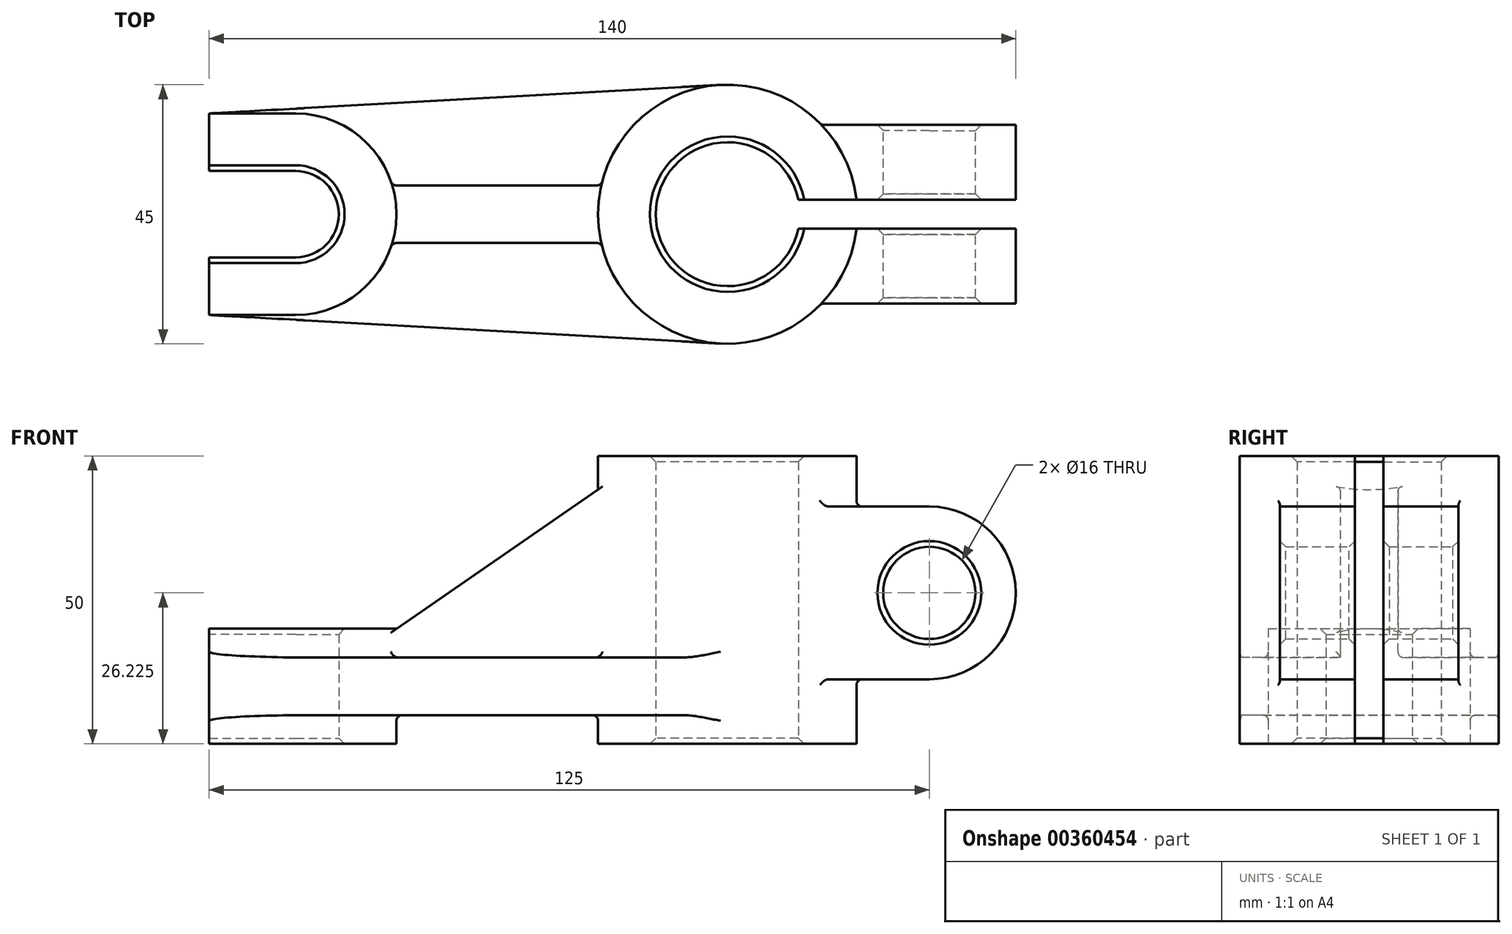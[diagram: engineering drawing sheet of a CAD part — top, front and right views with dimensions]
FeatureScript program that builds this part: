
annotation { "Feature Type Name" : "Feature", "Feature Type Description" : "" }
export const myFeature = defineFeature(function(context is Context, id is Id, definition is map)
    precondition{}
    {
        {
            var Q0;
            Q0=qCreatedBy(makeId("Top.planeOp"),FACE);
            var sketch = newSketch(context, id + "F0", { "sketchPlane" : qUnion([Q0])});
            skCircle(sketch, "E0", {"center": v(0, 0) * mm, "radius": 22.5 * mm});
            skCircle(sketch, "E1", {"center": v(0, 0) * mm, "radius": 12.5 * mm});
            skLineSegment(sketch, "E2", {"start": v(0, 0) * mm, "end": v(-75, 0) * mm, "construction": true});
            skArc(sketch, "E3", {"start": v(-75, -17.5) * mm, "mid": v(-57.5, 0) * mm, "end": v(-75, 17.5) * mm});
            skArc(sketch, "E4", {"start": v(-75, -7.5) * mm, "mid": v(-67.5, 0) * mm, "end": v(-75, 7.5) * mm});
            skLineSegment(sketch, "E5", {"start": v(-75, 17.5) * mm, "end": v(-90, 17.5) * mm});
            skLineSegment(sketch, "E6", {"start": v(-75, 7.5) * mm, "end": v(-90, 7.5) * mm});
            skLineSegment(sketch, "E7", {"start": v(-90, 17.5) * mm, "end": v(-90, 7.5) * mm});
            skLineSegment(sketch, "E8.MirrorCS", {"start": v(-75, -17.5) * mm, "end": v(-90, -17.5) * mm});
            skLineSegment(sketch, "E9.MirrorCS", {"start": v(-90, -17.5) * mm, "end": v(-90, -7.5) * mm});
            skLineSegment(sketch, "E10.MirrorCS", {"start": v(-75, -7.5) * mm, "end": v(-90, -7.5) * mm});
            skLineSegment(sketch, "E11", {"start": v(-90, 17.5) * mm, "end": v(-1.26, 22.46) * mm});
            skLineSegment(sketch, "E12.MirrorCS", {"start": v(-90, -17.5) * mm, "end": v(-1.26, -22.46) * mm});
            skSolve(sketch);
        }
        {
            var Q0;
            Q0 = qSketchRegion(id + "F0", true);
            extrude(context, id + "F1", {"entities" : qUnion([Q0]), "depth" : 10 * mm});
        }
        {
            var Q0;
            Q0=makeQuery(id+"F1.opExtrude","CAP_FACE",FACE,{"disambiguationData":[OSD([sQuery(id+"F0.wireOp",EDGE,"E0"),sQuery(id+"F0.wireOp",EDGE,"E1"),sQuery(id+"F0.wireOp",EDGE,"E4"),sQuery(id+"F0.wireOp",EDGE,"E6"),sQuery(id+"F0.wireOp",EDGE,"E7"),sQuery(id+"F0.wireOp",EDGE,"E9.MirrorCS"),sQuery(id+"F0.wireOp",EDGE,"E10.MirrorCS"),sQuery(id+"F0.wireOp",EDGE,"E11"),sQuery(id+"F0.wireOp",EDGE,"E12.MirrorCS")])],"isStart":false});
            var sketch = newSketch(context, id + "F2", { "sketchPlane" : qUnion([Q0])});
            skArc(sketch, "E13", {"start": v(-75, -17.5) * mm, "mid": v(-57.5, 0) * mm, "end": v(-75, 17.5) * mm});
            skArc(sketch, "E14.0", {"start": v(-75, -7.5) * mm, "mid": v(-67.5, 0) * mm, "end": v(-75, 7.5) * mm});
            skLineSegment(sketch, "E15", {"start": v(-75, 7.5) * mm, "end": v(-90, 7.5) * mm});
            skLineSegment(sketch, "E16", {"start": v(-90, 7.5) * mm, "end": v(-90, 17.5) * mm});
            skLineSegment(sketch, "E17", {"start": v(-90, 17.5) * mm, "end": v(-75, 17.5) * mm});
            skLineSegment(sketch, "E18", {"start": v(-75, 0) * mm, "end": v(0, 0) * mm, "construction": true});
            skLineSegment(sketch, "E19.MirrorCS", {"start": v(-90, -17.5) * mm, "end": v(-75, -17.5) * mm});
            skLineSegment(sketch, "E20.MirrorCS", {"start": v(-90, -7.5) * mm, "end": v(-90, -17.5) * mm});
            skLineSegment(sketch, "E21.MirrorCS", {"start": v(-75, -7.5) * mm, "end": v(-90, -7.5) * mm});
            skSolve(sketch);
        }
        {
            var Q0;
            Q0 = qSketchRegion(id + "F2", true);
            extrude(context, id + "F3", {"entities" : qUnion([Q0]), "operationType" : NewBodyOperationType.ADD, "depth" : 5 * mm, "hasSecondDirection" : true, "secondDirectionOppositeDirection" : true, "secondDirectionDepth" : 15 * mm});
        }
        {
            var Q0;
            Q0=makeQuery(id+"F1.opExtrude","CAP_FACE",FACE,{"disambiguationData":[OSD([sQuery(id+"F0.wireOp",EDGE,"E0"),sQuery(id+"F0.wireOp",EDGE,"E1"),sQuery(id+"F0.wireOp",EDGE,"E4"),sQuery(id+"F0.wireOp",EDGE,"E6"),sQuery(id+"F0.wireOp",EDGE,"E7"),sQuery(id+"F0.wireOp",EDGE,"E9.MirrorCS"),sQuery(id+"F0.wireOp",EDGE,"E10.MirrorCS"),sQuery(id+"F0.wireOp",EDGE,"E11"),sQuery(id+"F0.wireOp",EDGE,"E12.MirrorCS")])],"isStart":false});
            var sketch = newSketch(context, id + "F4", { "sketchPlane" : qUnion([Q0])});
            skCircle(sketch, "E22", {"center": v(0, 0) * mm, "radius": 22.5 * mm});
            skCircle(sketch, "E23", {"center": v(0, 0) * mm, "radius": 12.5 * mm});
            skSolve(sketch);
        }
        {
            var Q0;
            Q0 = qSketchRegion(id + "F4", true);
            extrude(context, id + "F5", {"entities" : qUnion([Q0]), "operationType" : NewBodyOperationType.ADD, "depth" : 35 * mm, "hasSecondDirection" : true, "secondDirectionOppositeDirection" : true, "secondDirectionDepth" : 15 * mm});
        }
        {
            var Q0;
            Q0=qCreatedBy(makeId("Front.planeOp"),FACE);
            var sketch = newSketch(context, id + "F6", { "sketchPlane" : qUnion([Q0])});
            skLineSegment(sketch, "E24", {"start": v(12.5, 36.22) * mm, "end": v(12.5, 6.22) * mm});
            skLineSegment(sketch, "E25", {"start": v(12.5, 36.22) * mm, "end": v(35, 36.22) * mm});
            skLineSegment(sketch, "E26", {"start": v(35, 36.22) * mm, "end": v(35, 21.22) * mm, "construction": true});
            skArc(sketch, "E27", {"start": v(35, 6.22) * mm, "mid": v(50, 21.22) * mm, "end": v(35, 36.22) * mm});
            skCircle(sketch, "E28", {"center": v(35, 21.22) * mm, "radius": 8 * mm});
            skLineSegment(sketch, "E29", {"start": v(35, 6.22) * mm, "end": v(12.5, 6.22) * mm});
            skSolve(sketch);
        }
        {
            var Q0;
            Q0 = qSketchRegion(id + "F6", true);
            extrude(context, id + "F7", {"entities" : qUnion([Q0]), "operationType" : NewBodyOperationType.ADD, "endBound" : BoundingType.SYMMETRIC, "depth" : 31 * mm});
        }
        {
            var Q0;
            Q0=qCreatedBy(makeId("Right.planeOp"),FACE);
            var sketch = newSketch(context, id + "F8", { "sketchPlane" : qUnion([Q0])});
            skPoint(sketch, "E30.0", {"position": v(0, 0) * mm});
            skLineSegment(sketch, "E31", {"start": v(0, 0) * mm, "end": v(0, 60.52) * mm, "construction": true});
            skLineSegment(sketch, "E32", {"start": v(0, 0) * mm, "end": v(0, -26.54) * mm, "construction": true});
            skLineSegment(sketch, "E33.0", {"start": v(-2.5, 45) * mm, "end": v(2.5, 45) * mm});
            skLineSegment(sketch, "E34", {"start": v(0, 45) * mm, "end": v(2.5, 45) * mm});
            skLineSegment(sketch, "E35", {"start": v(2.5, 45) * mm, "end": v(2.5, -5) * mm});
            skLineSegment(sketch, "E36", {"start": v(2.5, -5) * mm, "end": v(-2.5, -5) * mm});
            skLineSegment(sketch, "E37", {"start": v(-2.5, -5) * mm, "end": v(-2.5, 45) * mm});
            skLineSegment(sketch, "E38", {"start": v(-2.5, 45) * mm, "end": v(0, 45) * mm});
            skPoint(sketch, "E39.orphan", {"position": v(-22.5, 45) * mm});
            skPoint(sketch, "E40.orphan", {"position": v(22.5, 45) * mm});
            skSolve(sketch);
        }
        {
            var Q0;
            Q0 = qSketchRegion(id + "F8", true);
            extrude(context, id + "F9", {"entities" : qUnion([Q0]), "operationType" : NewBodyOperationType.REMOVE, "endBound" : BoundingType.THROUGH_ALL, "depth" : 25 * mm});
        }
        {
            var Q0;
            Q0=qCreatedBy(makeId("Front.planeOp"),FACE);
            var sketch = newSketch(context, id + "F10", { "sketchPlane" : qUnion([Q0])});
            skLineSegment(sketch, "E41", {"start": v(-22.5, 39.17) * mm, "end": v(-22.5, 39.22) * mm});
            skLineSegment(sketch, "E42", {"start": v(-57.5, 15) * mm, "end": v(-57.5, 15) * mm});
            skLineSegment(sketch, "E43", {"start": v(-64.73, 10) * mm, "end": v(-22.5, 10) * mm});
            skLineSegment(sketch, "E44", {"start": v(-22.5, 10) * mm, "end": v(-19.86, 10) * mm});
            skLineSegment(sketch, "E45", {"start": v(-19.86, 10) * mm, "end": v(-19.86, 41) * mm});
            skPoint(sketch, "E46.end.orphan", {"position": v(-22.5, 39.22) * mm});
            skLineSegment(sketch, "E47", {"start": v(-19.86, 41) * mm, "end": v(-64.73, 10) * mm});
            skPoint(sketch, "E48.orphan", {"position": v(-57.5, 10) * mm});
            skSolve(sketch);
        }
        {
            var Q0;
            Q0 = qSketchRegion(id + "F10", true);
            extrude(context, id + "F11", {"entities" : qUnion([Q0]), "operationType" : NewBodyOperationType.ADD, "endBound" : BoundingType.SYMMETRIC, "depth" : 10 * mm});
        }
        {
            var Q0;
            Q0=makeQuery(id+"F11.opExtrude","CAP_EDGE",EDGE,{"disambiguationData":[OSD([sQuery(id+"F10.wireOp",EDGE,"E43"),sQuery(id+"F10.wireOp",EDGE,"E44")])],"isStart":false});
            var Q1;
            {var subQ0=makeQuery(id+"F1.opExtrude","CAP_FACE",FACE,{"disambiguationData":[OSD([sQuery(id+"F0.wireOp",EDGE,"E0"),sQuery(id+"F0.wireOp",EDGE,"E1"),sQuery(id+"F0.wireOp",EDGE,"E4"),sQuery(id+"F0.wireOp",EDGE,"E6"),sQuery(id+"F0.wireOp",EDGE,"E7"),sQuery(id+"F0.wireOp",EDGE,"E9.MirrorCS"),sQuery(id+"F0.wireOp",EDGE,"E10.MirrorCS"),sQuery(id+"F0.wireOp",EDGE,"E11"),sQuery(id+"F0.wireOp",EDGE,"E12.MirrorCS")])],"isStart":false});var subQ1=makeQuery(id+"F3.opExtrude","SWEPT_FACE",FACE,{"disambiguationData":[OSD([sQuery(id+"F2.wireOp",EDGE,"E13")])]});Q1=makeQuery(id+"F11.boolean.opBoolean","SPLIT",EDGE,{"disambiguationData":[TD([makeQuery(id+"F3.opExtrude","SWEPT_FACE",FACE,{"disambiguationData":[OSD([sQuery(id+"F2.wireOp",EDGE,"E19.MirrorCS")])]})])],"derivedFrom":makeQuery(id+"F3.boolean.opBoolean","INTERSECT",EDGE,{"derivedFrom":[subQ0,subQ1]})});}
            var Q2;
            {var subQ0=sQuery(id+"F2.wireOp",EDGE,"E19.MirrorCS");var subQ1=sQuery(id+"F2.wireOp",EDGE,"E17");var subQ2=sQuery(id+"F2.wireOp",EDGE,"E13");Q2=makeQuery(id+"F11.boolean.opBoolean","INTERSECT",EDGE,{"derivedFrom":[makeQuery(id+"F3.boolean.opBoolean","SPLIT",FACE,{"disambiguationData":[TD([makeQuery(id+"F3.opExtrude","CAP_FACE",FACE,{"disambiguationData":[OSD([subQ2,sQuery(id+"F2.wireOp",EDGE,"E14.0"),sQuery(id+"F2.wireOp",EDGE,"E15"),sQuery(id+"F2.wireOp",EDGE,"E16"),subQ1,subQ0,sQuery(id+"F2.wireOp",EDGE,"E20.MirrorCS"),sQuery(id+"F2.wireOp",EDGE,"E21.MirrorCS")])],"isStart":false})])],"derivedFrom":makeQuery(id+"F3.opExtrude","SWEPT_FACE",FACE,{"disambiguationData":[OSD([subQ2])]})}),makeQuery(id+"F11.opExtrude","CAP_FACE",FACE,{"disambiguationData":[OSD([sQuery(id+"F10.wireOp",EDGE,"E43"),sQuery(id+"F10.wireOp",EDGE,"E44"),sQuery(id+"F10.wireOp",EDGE,"E45"),sQuery(id+"F10.wireOp",EDGE,"E47")])],"isStart":false})]});}
            var Q3;
            Q3=makeQuery(id+"F11.boolean.opBoolean","INTERSECT",EDGE,{"derivedFrom":[makeQuery(id+"F5.boolean.opBoolean","MERGE",FACE,{"derivedFrom":[makeQuery(id+"F1.opExtrude","SWEPT_FACE",FACE,{"disambiguationData":[OSD([sQuery(id+"F0.wireOp",EDGE,"E0")])]}),makeQuery(id+"F5.opExtrude","SWEPT_FACE",FACE,{"disambiguationData":[OSD([sQuery(id+"F4.wireOp",EDGE,"E22")])]})]}),makeQuery(id+"F11.opExtrude","CAP_FACE",FACE,{"disambiguationData":[OSD([sQuery(id+"F10.wireOp",EDGE,"E43"),sQuery(id+"F10.wireOp",EDGE,"E44"),sQuery(id+"F10.wireOp",EDGE,"E45"),sQuery(id+"F10.wireOp",EDGE,"E47")])],"isStart":false})]});
            var Q4;
            {var subQ0=makeQuery(id+"F5.opExtrude","SWEPT_FACE",FACE,{"disambiguationData":[OSD([sQuery(id+"F4.wireOp",EDGE,"E22")])]});var subQ1=sQuery(id+"F0.wireOp",EDGE,"E12.MirrorCS");var subQ2=sQuery(id+"F0.wireOp",EDGE,"E0");var subQ3=makeQuery(id+"F1.opExtrude","CAP_FACE",FACE,{"disambiguationData":[OSD([subQ2,sQuery(id+"F0.wireOp",EDGE,"E1"),sQuery(id+"F0.wireOp",EDGE,"E4"),sQuery(id+"F0.wireOp",EDGE,"E6"),sQuery(id+"F0.wireOp",EDGE,"E7"),sQuery(id+"F0.wireOp",EDGE,"E9.MirrorCS"),sQuery(id+"F0.wireOp",EDGE,"E10.MirrorCS"),sQuery(id+"F0.wireOp",EDGE,"E11"),subQ1])],"isStart":false});Q4=makeQuery(id+"F11.boolean.opBoolean","SPLIT",EDGE,{"disambiguationData":[TD([makeQuery(id+"F1.opExtrude","SWEPT_FACE",FACE,{"disambiguationData":[OSD([subQ1])]})])],"derivedFrom":makeQuery(id+"F5.boolean.opBoolean","INTERSECT",EDGE,{"derivedFrom":[subQ3,subQ0]})});}
            var Q5;
            {var subQ0=sQuery(id+"F0.wireOp",EDGE,"E11");var subQ1=makeQuery(id+"F5.opExtrude","SWEPT_FACE",FACE,{"disambiguationData":[OSD([sQuery(id+"F4.wireOp",EDGE,"E22")])]});var subQ2=sQuery(id+"F0.wireOp",EDGE,"E0");var subQ3=makeQuery(id+"F1.opExtrude","CAP_FACE",FACE,{"disambiguationData":[OSD([subQ2,sQuery(id+"F0.wireOp",EDGE,"E1"),sQuery(id+"F0.wireOp",EDGE,"E4"),sQuery(id+"F0.wireOp",EDGE,"E6"),sQuery(id+"F0.wireOp",EDGE,"E7"),sQuery(id+"F0.wireOp",EDGE,"E9.MirrorCS"),sQuery(id+"F0.wireOp",EDGE,"E10.MirrorCS"),subQ0,sQuery(id+"F0.wireOp",EDGE,"E12.MirrorCS")])],"isStart":false});Q5=makeQuery(id+"F11.boolean.opBoolean","SPLIT",EDGE,{"disambiguationData":[TD([makeQuery(id+"F1.opExtrude","SWEPT_FACE",FACE,{"disambiguationData":[OSD([subQ0])]})])],"derivedFrom":makeQuery(id+"F5.boolean.opBoolean","INTERSECT",EDGE,{"derivedFrom":[subQ3,subQ1]})});}
            var Q6;
            Q6=makeQuery(id+"F11.boolean.opBoolean","INTERSECT",EDGE,{"derivedFrom":[makeQuery(id+"F5.boolean.opBoolean","MERGE",FACE,{"derivedFrom":[makeQuery(id+"F1.opExtrude","SWEPT_FACE",FACE,{"disambiguationData":[OSD([sQuery(id+"F0.wireOp",EDGE,"E0")])]}),makeQuery(id+"F5.opExtrude","SWEPT_FACE",FACE,{"disambiguationData":[OSD([sQuery(id+"F4.wireOp",EDGE,"E22")])]})]}),makeQuery(id+"F11.opExtrude","CAP_FACE",FACE,{"disambiguationData":[OSD([sQuery(id+"F10.wireOp",EDGE,"E43"),sQuery(id+"F10.wireOp",EDGE,"E44"),sQuery(id+"F10.wireOp",EDGE,"E45"),sQuery(id+"F10.wireOp",EDGE,"E47")])],"isStart":true})]});
            var Q7;
            Q7=makeQuery(id+"F11.opExtrude","CAP_EDGE",EDGE,{"disambiguationData":[OSD([sQuery(id+"F10.wireOp",EDGE,"E43"),sQuery(id+"F10.wireOp",EDGE,"E44")])],"isStart":true});
            var Q8;
            {var subQ0=makeQuery(id+"F1.opExtrude","CAP_FACE",FACE,{"disambiguationData":[OSD([sQuery(id+"F0.wireOp",EDGE,"E0"),sQuery(id+"F0.wireOp",EDGE,"E1"),sQuery(id+"F0.wireOp",EDGE,"E4"),sQuery(id+"F0.wireOp",EDGE,"E6"),sQuery(id+"F0.wireOp",EDGE,"E7"),sQuery(id+"F0.wireOp",EDGE,"E9.MirrorCS"),sQuery(id+"F0.wireOp",EDGE,"E10.MirrorCS"),sQuery(id+"F0.wireOp",EDGE,"E11"),sQuery(id+"F0.wireOp",EDGE,"E12.MirrorCS")])],"isStart":false});var subQ1=makeQuery(id+"F3.opExtrude","SWEPT_FACE",FACE,{"disambiguationData":[OSD([sQuery(id+"F2.wireOp",EDGE,"E13")])]});Q8=makeQuery(id+"F11.boolean.opBoolean","SPLIT",EDGE,{"disambiguationData":[TD([makeQuery(id+"F3.opExtrude","SWEPT_FACE",FACE,{"disambiguationData":[OSD([sQuery(id+"F2.wireOp",EDGE,"E17")])]})])],"derivedFrom":makeQuery(id+"F3.boolean.opBoolean","INTERSECT",EDGE,{"derivedFrom":[subQ0,subQ1]})});}
            var Q9;
            {var subQ0=sQuery(id+"F2.wireOp",EDGE,"E19.MirrorCS");var subQ1=sQuery(id+"F2.wireOp",EDGE,"E17");var subQ2=sQuery(id+"F2.wireOp",EDGE,"E13");Q9=makeQuery(id+"F11.boolean.opBoolean","INTERSECT",EDGE,{"derivedFrom":[makeQuery(id+"F3.boolean.opBoolean","SPLIT",FACE,{"disambiguationData":[TD([makeQuery(id+"F3.opExtrude","CAP_FACE",FACE,{"disambiguationData":[OSD([subQ2,sQuery(id+"F2.wireOp",EDGE,"E14.0"),sQuery(id+"F2.wireOp",EDGE,"E15"),sQuery(id+"F2.wireOp",EDGE,"E16"),subQ1,subQ0,sQuery(id+"F2.wireOp",EDGE,"E20.MirrorCS"),sQuery(id+"F2.wireOp",EDGE,"E21.MirrorCS")])],"isStart":false})])],"derivedFrom":makeQuery(id+"F3.opExtrude","SWEPT_FACE",FACE,{"disambiguationData":[OSD([subQ2])]})}),makeQuery(id+"F11.opExtrude","CAP_FACE",FACE,{"disambiguationData":[OSD([sQuery(id+"F10.wireOp",EDGE,"E43"),sQuery(id+"F10.wireOp",EDGE,"E44"),sQuery(id+"F10.wireOp",EDGE,"E45"),sQuery(id+"F10.wireOp",EDGE,"E47")])],"isStart":true})]});}
            var Q10;
            Q10=makeQuery(id+"F3.boolean.opBoolean","INTERSECT",EDGE,{"derivedFrom":[makeQuery(id+"F1.opExtrude","CAP_FACE",FACE,{"disambiguationData":[OSD([sQuery(id+"F0.wireOp",EDGE,"E0"),sQuery(id+"F0.wireOp",EDGE,"E1"),sQuery(id+"F0.wireOp",EDGE,"E4"),sQuery(id+"F0.wireOp",EDGE,"E6"),sQuery(id+"F0.wireOp",EDGE,"E7"),sQuery(id+"F0.wireOp",EDGE,"E9.MirrorCS"),sQuery(id+"F0.wireOp",EDGE,"E10.MirrorCS"),sQuery(id+"F0.wireOp",EDGE,"E11"),sQuery(id+"F0.wireOp",EDGE,"E12.MirrorCS")])],"isStart":true}),makeQuery(id+"F3.opExtrude","SWEPT_FACE",FACE,{"disambiguationData":[OSD([sQuery(id+"F2.wireOp",EDGE,"E13")])]})]});
            var Q11;
            Q11=makeQuery(id+"F5.boolean.opBoolean","INTERSECT",EDGE,{"derivedFrom":[makeQuery(id+"F1.opExtrude","CAP_FACE",FACE,{"disambiguationData":[OSD([sQuery(id+"F0.wireOp",EDGE,"E0"),sQuery(id+"F0.wireOp",EDGE,"E1"),sQuery(id+"F0.wireOp",EDGE,"E4"),sQuery(id+"F0.wireOp",EDGE,"E6"),sQuery(id+"F0.wireOp",EDGE,"E7"),sQuery(id+"F0.wireOp",EDGE,"E9.MirrorCS"),sQuery(id+"F0.wireOp",EDGE,"E10.MirrorCS"),sQuery(id+"F0.wireOp",EDGE,"E11"),sQuery(id+"F0.wireOp",EDGE,"E12.MirrorCS")])],"isStart":true}),makeQuery(id+"F5.opExtrude","SWEPT_FACE",FACE,{"disambiguationData":[OSD([sQuery(id+"F4.wireOp",EDGE,"E22")])]})]});
            var Q12;
            {var subQ0=sQuery(id+"F6.wireOp",EDGE,"E29");var subQ1=makeQuery(id+"F7.opExtrude","SWEPT_FACE",FACE,{"disambiguationData":[OSD([subQ0])]});var subQ2=makeQuery(id+"F5.opExtrude","SWEPT_FACE",FACE,{"disambiguationData":[OSD([sQuery(id+"F4.wireOp",EDGE,"E22")])]});var subQ3=makeQuery(id+"F1.opExtrude","SWEPT_FACE",FACE,{"disambiguationData":[OSD([sQuery(id+"F0.wireOp",EDGE,"E0")])]});Q12=makeQuery(id+"F9.boolean.opBoolean","SPLIT",EDGE,{"disambiguationData":[TD([makeQuery(id+"F9.opExtrude","SWEPT_FACE",FACE,{"disambiguationData":[OSD([sQuery(id+"F8.wireOp",EDGE,"E37")])]})])],"derivedFrom":makeQuery(id+"F7.boolean.opBoolean","INTERSECT",EDGE,{"derivedFrom":[makeQuery(id+"F5.boolean.opBoolean","MERGE",FACE,{"derivedFrom":[subQ3,subQ2]}),subQ1]})});}
            var Q13;
            {var subQ0=sQuery(id+"F6.wireOp",EDGE,"E29");var subQ1=makeQuery(id+"F7.opExtrude","SWEPT_FACE",FACE,{"disambiguationData":[OSD([subQ0])]});var subQ2=makeQuery(id+"F5.opExtrude","SWEPT_FACE",FACE,{"disambiguationData":[OSD([sQuery(id+"F4.wireOp",EDGE,"E22")])]});var subQ3=makeQuery(id+"F1.opExtrude","SWEPT_FACE",FACE,{"disambiguationData":[OSD([sQuery(id+"F0.wireOp",EDGE,"E0")])]});Q13=makeQuery(id+"F9.boolean.opBoolean","SPLIT",EDGE,{"disambiguationData":[TD([makeQuery(id+"F9.opExtrude","SWEPT_FACE",FACE,{"disambiguationData":[OSD([sQuery(id+"F8.wireOp",EDGE,"E35")])]})])],"derivedFrom":makeQuery(id+"F7.boolean.opBoolean","INTERSECT",EDGE,{"derivedFrom":[makeQuery(id+"F5.boolean.opBoolean","MERGE",FACE,{"derivedFrom":[subQ3,subQ2]}),subQ1]})});}
            var Q14;
            Q14=makeQuery(id+"F7.boolean.opBoolean","INTERSECT",EDGE,{"derivedFrom":[makeQuery(id+"F5.boolean.opBoolean","MERGE",FACE,{"derivedFrom":[makeQuery(id+"F1.opExtrude","SWEPT_FACE",FACE,{"disambiguationData":[OSD([sQuery(id+"F0.wireOp",EDGE,"E0")])]}),makeQuery(id+"F5.opExtrude","SWEPT_FACE",FACE,{"disambiguationData":[OSD([sQuery(id+"F4.wireOp",EDGE,"E22")])]})]}),makeQuery(id+"F7.opExtrude","CAP_FACE",FACE,{"disambiguationData":[OSD([sQuery(id+"F6.wireOp",EDGE,"E24"),sQuery(id+"F6.wireOp",EDGE,"E25"),sQuery(id+"F6.wireOp",EDGE,"E27"),sQuery(id+"F6.wireOp",EDGE,"E28"),sQuery(id+"F6.wireOp",EDGE,"E29")])],"isStart":true})]});
            var Q15;
            {var subQ0=sQuery(id+"F6.wireOp",EDGE,"E25");var subQ1=makeQuery(id+"F7.opExtrude","SWEPT_FACE",FACE,{"disambiguationData":[OSD([subQ0])]});var subQ2=makeQuery(id+"F5.opExtrude","SWEPT_FACE",FACE,{"disambiguationData":[OSD([sQuery(id+"F4.wireOp",EDGE,"E22")])]});var subQ3=makeQuery(id+"F1.opExtrude","SWEPT_FACE",FACE,{"disambiguationData":[OSD([sQuery(id+"F0.wireOp",EDGE,"E0")])]});Q15=makeQuery(id+"F9.boolean.opBoolean","SPLIT",EDGE,{"disambiguationData":[TD([makeQuery(id+"F9.opExtrude","SWEPT_FACE",FACE,{"disambiguationData":[OSD([sQuery(id+"F8.wireOp",EDGE,"E35")])]})])],"derivedFrom":makeQuery(id+"F7.boolean.opBoolean","INTERSECT",EDGE,{"derivedFrom":[makeQuery(id+"F5.boolean.opBoolean","MERGE",FACE,{"derivedFrom":[subQ3,subQ2]}),subQ1]})});}
            var Q16;
            {var subQ0=sQuery(id+"F6.wireOp",EDGE,"E25");var subQ1=makeQuery(id+"F7.opExtrude","SWEPT_FACE",FACE,{"disambiguationData":[OSD([subQ0])]});var subQ2=makeQuery(id+"F5.opExtrude","SWEPT_FACE",FACE,{"disambiguationData":[OSD([sQuery(id+"F4.wireOp",EDGE,"E22")])]});var subQ3=makeQuery(id+"F1.opExtrude","SWEPT_FACE",FACE,{"disambiguationData":[OSD([sQuery(id+"F0.wireOp",EDGE,"E0")])]});Q16=makeQuery(id+"F9.boolean.opBoolean","SPLIT",EDGE,{"disambiguationData":[TD([makeQuery(id+"F9.opExtrude","SWEPT_FACE",FACE,{"disambiguationData":[OSD([sQuery(id+"F8.wireOp",EDGE,"E37")])]})])],"derivedFrom":makeQuery(id+"F7.boolean.opBoolean","INTERSECT",EDGE,{"derivedFrom":[makeQuery(id+"F5.boolean.opBoolean","MERGE",FACE,{"derivedFrom":[subQ3,subQ2]}),subQ1]})});}
            var Q17;
            Q17=makeQuery(id+"F7.boolean.opBoolean","INTERSECT",EDGE,{"derivedFrom":[makeQuery(id+"F5.boolean.opBoolean","MERGE",FACE,{"derivedFrom":[makeQuery(id+"F1.opExtrude","SWEPT_FACE",FACE,{"disambiguationData":[OSD([sQuery(id+"F0.wireOp",EDGE,"E0")])]}),makeQuery(id+"F5.opExtrude","SWEPT_FACE",FACE,{"disambiguationData":[OSD([sQuery(id+"F4.wireOp",EDGE,"E22")])]})]}),makeQuery(id+"F7.opExtrude","CAP_FACE",FACE,{"disambiguationData":[OSD([sQuery(id+"F6.wireOp",EDGE,"E24"),sQuery(id+"F6.wireOp",EDGE,"E25"),sQuery(id+"F6.wireOp",EDGE,"E27"),sQuery(id+"F6.wireOp",EDGE,"E28"),sQuery(id+"F6.wireOp",EDGE,"E29")])],"isStart":false})]});
            fillet(context, id + "F12", {"entities" : qUnion([Q0, Q1, Q2, Q3, Q4, Q5, Q6, Q7, Q8, Q9, Q10, Q11, Q12, Q13, Q14, Q15, Q16, Q17]), "radius" : 1 * mm, "tangentPropagation" : true, "allowEdgeOverflow" : false});
        }
        {
            var Q0;
            Q0=makeQuery(id+"F5.opExtrude","CAP_EDGE",EDGE,{"disambiguationData":[OSD([sQuery(id+"F4.wireOp",EDGE,"E23")])],"isStart":false});
            var Q1;
            Q1=makeQuery(id+"F7.opExtrude","CAP_EDGE",EDGE,{"disambiguationData":[OSD([sQuery(id+"F6.wireOp",EDGE,"E28")])],"isStart":true});
            var Q2;
            Q2=makeQuery(id+"F7.opExtrude","CAP_EDGE",EDGE,{"disambiguationData":[OSD([sQuery(id+"F6.wireOp",EDGE,"E28")])],"isStart":false});
            var Q3;
            Q3=makeQuery(id+"F9.boolean.opBoolean","INTERSECT",EDGE,{"derivedFrom":[makeQuery(id+"F7.opExtrude","SWEPT_FACE",FACE,{"disambiguationData":[OSD([sQuery(id+"F6.wireOp",EDGE,"E28")])]}),makeQuery(id+"F9.opExtrude","SWEPT_FACE",FACE,{"disambiguationData":[OSD([sQuery(id+"F8.wireOp",EDGE,"E37")])]})]});
            var Q4;
            Q4=makeQuery(id+"F9.boolean.opBoolean","INTERSECT",EDGE,{"derivedFrom":[makeQuery(id+"F7.opExtrude","SWEPT_FACE",FACE,{"disambiguationData":[OSD([sQuery(id+"F6.wireOp",EDGE,"E28")])]}),makeQuery(id+"F9.opExtrude","SWEPT_FACE",FACE,{"disambiguationData":[OSD([sQuery(id+"F8.wireOp",EDGE,"E35")])]})]});
            var Q5;
            Q5=makeQuery(id+"F5.opExtrude","CAP_EDGE",EDGE,{"disambiguationData":[OSD([sQuery(id+"F4.wireOp",EDGE,"E23")])],"isStart":true});
            var Q6;
            Q6=makeQuery(id+"F3.opExtrude","CAP_EDGE",EDGE,{"disambiguationData":[OSD([sQuery(id+"F2.wireOp",EDGE,"E15")])],"isStart":false});
            var Q7;
            Q7=makeQuery(id+"F3.opExtrude","CAP_EDGE",EDGE,{"disambiguationData":[OSD([sQuery(id+"F2.wireOp",EDGE,"E14.0")])],"isStart":false});
            var Q8;
            Q8=makeQuery(id+"F3.opExtrude","CAP_EDGE",EDGE,{"disambiguationData":[OSD([sQuery(id+"F2.wireOp",EDGE,"E21.MirrorCS")])],"isStart":false});
            var Q9;
            Q9=makeQuery(id+"F3.opExtrude","CAP_EDGE",EDGE,{"disambiguationData":[OSD([sQuery(id+"F2.wireOp",EDGE,"E15")])],"isStart":true});
            var Q10;
            Q10=makeQuery(id+"F3.opExtrude","CAP_EDGE",EDGE,{"disambiguationData":[OSD([sQuery(id+"F2.wireOp",EDGE,"E14.0")])],"isStart":true});
            var Q11;
            Q11=makeQuery(id+"F3.opExtrude","CAP_EDGE",EDGE,{"disambiguationData":[OSD([sQuery(id+"F2.wireOp",EDGE,"E21.MirrorCS")])],"isStart":true});
            chamfer(context, id + "F13", {"entities" : qUnion([Q0, Q1, Q2, Q3, Q4, Q5, Q6, Q7, Q8, Q9, Q10, Q11]), "width" : 1 * mm, "tangentPropagation" : true});
        }
    });
